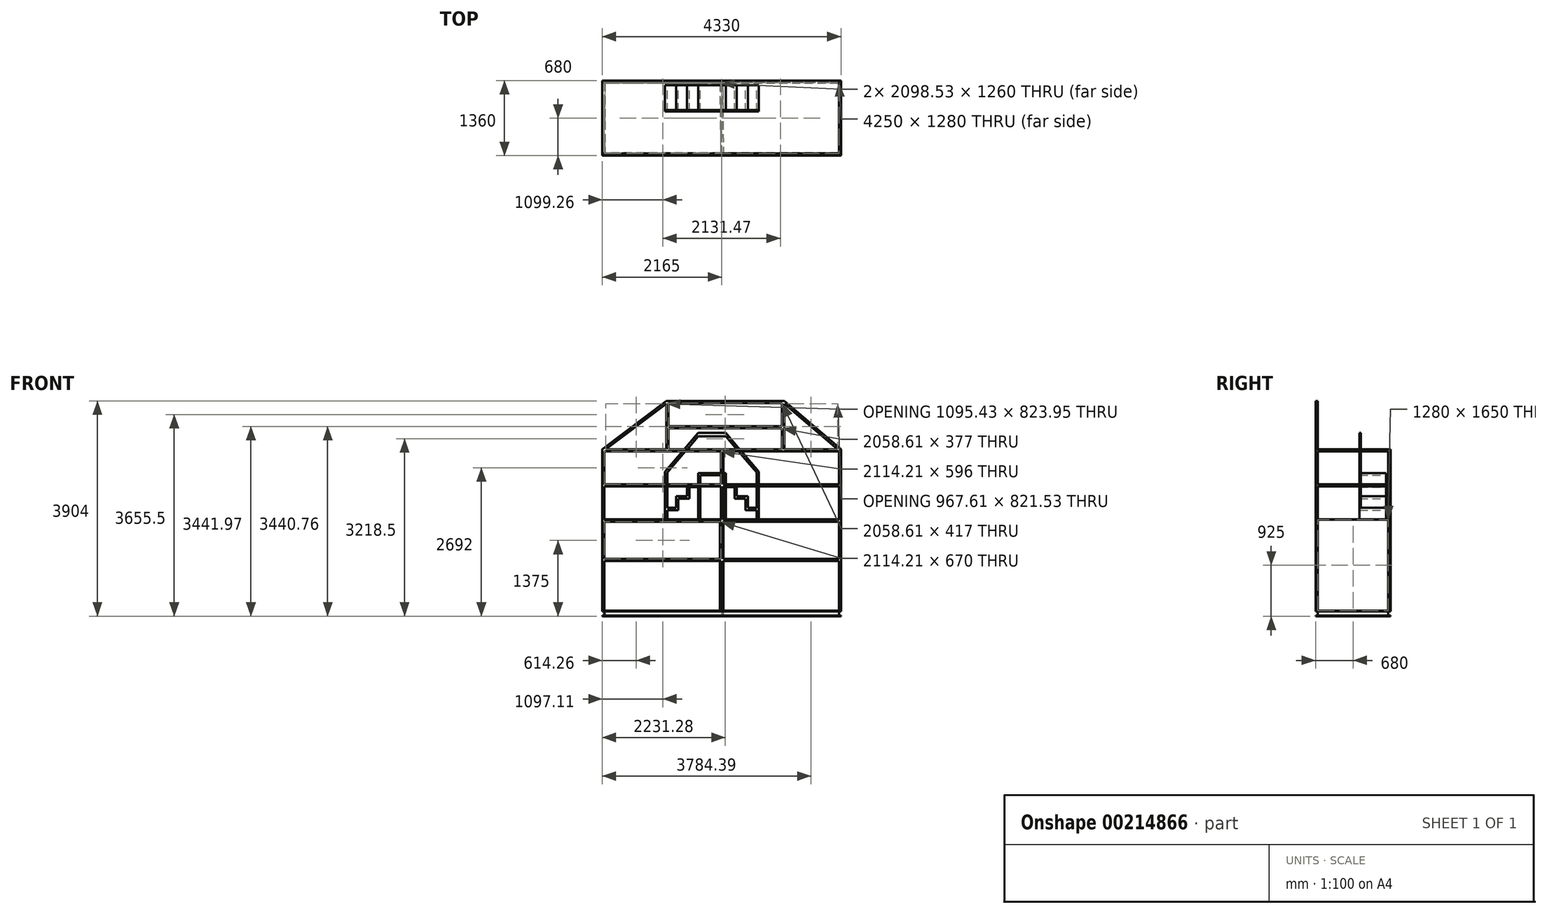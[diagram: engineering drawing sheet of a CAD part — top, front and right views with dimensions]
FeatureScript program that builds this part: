
annotation { "Feature Type Name" : "Feature", "Feature Type Description" : "" }
export const myFeature = defineFeature(function(context is Context, id is Id, definition is map)
    precondition{}
    {
        {
            var Q0;
            Q0=qCreatedBy(makeId("Top.planeOp"),FACE);
            var sketch = newSketch(context, id + "F0", { "sketchPlane" : qUnion([Q0])});
            skLineSegment(sketch, "E0.rect.bottom", {"start": v(2165, 680) * mm, "end": v(-2165, 680) * mm});
            skLineSegment(sketch, "E0.rect.top", {"start": v(2165, -680) * mm, "end": v(-2165, -680) * mm});
            skLineSegment(sketch, "E0.rect.left", {"start": v(2165, 680) * mm, "end": v(2165, -680) * mm});
            skLineSegment(sketch, "E0.rect.right", {"start": v(-2165, 680) * mm, "end": v(-2165, -680) * mm});
            skPoint(sketch, "E0.rect.middle", {"position": v(0, 0) * mm});
            skLineSegment(sketch, "E1.rect.bottom", {"start": v(2115, 630) * mm, "end": v(16.47, 630) * mm});
            skLineSegment(sketch, "E1.rect.top", {"start": v(2115, -630) * mm, "end": v(33.53, -630) * mm});
            skLineSegment(sketch, "E1.rect.left", {"start": v(2115, 630) * mm, "end": v(2115, -630) * mm});
            skLineSegment(sketch, "E1.rect.right", {"start": v(-2115, 630) * mm, "end": v(-2115, -630) * mm});
            skLineSegment(sketch, "E2.rect.left", {"start": v(16.47, 630) * mm, "end": v(33.53, -630) * mm});
            skLineSegment(sketch, "E2.rect.right", {"start": v(-33.53, 630) * mm, "end": v(-16.47, -630) * mm});
            skLineSegment(sketch, "E3.trimOffspring", {"start": v(-33.53, 630) * mm, "end": v(-2115, 630) * mm});
            skLineSegment(sketch, "E4.trimOffspring", {"start": v(-16.47, -630) * mm, "end": v(-2115, -630) * mm});
            skSolve(sketch);
        }
        {
            var Q0;
            Q0=makeQuery(id+"F0.imprint","IMPRINT",FACE,{"disambiguationData":[TD([[makeQuery(id+"F0.imprint","IMPRINT",EDGE,{"derivedFrom":sQuery(id+"F0.wireOp",EDGE,"E0.rect.bottom")}),1.0]])]});
            extrude(context, id + "F1", {"entities" : qUnion([Q0]), "depth" : 100 * mm});
        }
        {
            var Q0;
            Q0=makeQuery(id+"F1.opExtrude","SWEPT_FACE",FACE,{"disambiguationData":[OSD([sQuery(id+"F0.wireOp",EDGE,"E0.rect.right")])]});
            var sketch = newSketch(context, id + "F2", { "sketchPlane" : qUnion([Q0])});
            skLineSegment(sketch, "E5.bottom", {"start": v(-680, 90) * mm, "end": v(-640, 90) * mm});
            skLineSegment(sketch, "E5.top", {"start": v(-680, 10) * mm, "end": v(-640, 10) * mm});
            skLineSegment(sketch, "E5.left", {"start": v(-680, 90) * mm, "end": v(-680, 10) * mm});
            skLineSegment(sketch, "E5.right", {"start": v(-640, 90) * mm, "end": v(-640, 10) * mm});
            skLineSegment(sketch, "E6.bottom", {"start": v(680, 90) * mm, "end": v(640, 90) * mm});
            skLineSegment(sketch, "E6.top", {"start": v(680, 10) * mm, "end": v(640, 10) * mm});
            skLineSegment(sketch, "E6.left", {"start": v(680, 90) * mm, "end": v(680, 10) * mm});
            skLineSegment(sketch, "E6.right", {"start": v(640, 90) * mm, "end": v(640, 10) * mm});
            skSolve(sketch);
        }
        {
            var Q0;
            Q0=makeQuery(id+"F2.imprint","IMPRINT",FACE,{"disambiguationData":[TD([[makeQuery(id+"F2.imprint","IMPRINT",EDGE,{"derivedFrom":sQuery(id+"F2.wireOp",EDGE,"E5.bottom")}),-1.0]])]});
            var Q1;
            Q1=makeQuery(id+"F2.imprint","IMPRINT",FACE,{"disambiguationData":[TD([[makeQuery(id+"F2.imprint","IMPRINT",EDGE,{"derivedFrom":sQuery(id+"F2.wireOp",EDGE,"E6.bottom")}),1.0]])]});
            extrude(context, id + "F3", {"entities" : qUnion([Q0, Q1]), "operationType" : NewBodyOperationType.REMOVE, "endBound" : BoundingType.THROUGH_ALL, "oppositeDirection" : true, "depth" : 25 * mm});
        }
        {
            var Q0;
            Q0=makeQuery(id+"F3.boolean.opBoolean","COPY",FACE,{"derivedFrom":makeQuery(id+"F3.opExtrude","SWEPT_FACE",FACE,{"disambiguationData":[OSD([sQuery(id+"F2.wireOp",EDGE,"E6.right")])]})});
            var sketch = newSketch(context, id + "F4", { "sketchPlane" : qUnion([Q0])});
            skLineSegment(sketch, "E7.bottom", {"start": v(2165, 90) * mm, "end": v(2125, 90) * mm});
            skLineSegment(sketch, "E7.top", {"start": v(2165, 10) * mm, "end": v(2125, 10) * mm});
            skLineSegment(sketch, "E7.left", {"start": v(2165, 90) * mm, "end": v(2165, 10) * mm});
            skLineSegment(sketch, "E7.right", {"start": v(2125, 90) * mm, "end": v(2125, 10) * mm});
            skLineSegment(sketch, "E8.bottom", {"start": v(-2165, 90) * mm, "end": v(-2125, 90) * mm});
            skLineSegment(sketch, "E8.top", {"start": v(-2165, 10) * mm, "end": v(-2125, 10) * mm});
            skLineSegment(sketch, "E8.left", {"start": v(-2165, 90) * mm, "end": v(-2165, 10) * mm});
            skLineSegment(sketch, "E8.right", {"start": v(-2125, 90) * mm, "end": v(-2125, 10) * mm});
            skSolve(sketch);
        }
        {
            var Q0;
            Q0=makeQuery(id+"F4.imprint","IMPRINT",FACE,{"disambiguationData":[TD([[makeQuery(id+"F4.imprint","IMPRINT",EDGE,{"derivedFrom":sQuery(id+"F4.wireOp",EDGE,"E7.bottom")}),1.0]])]});
            var Q1;
            Q1=makeQuery(id+"F4.imprint","IMPRINT",FACE,{"disambiguationData":[TD([[makeQuery(id+"F4.imprint","IMPRINT",EDGE,{"derivedFrom":sQuery(id+"F4.wireOp",EDGE,"E8.bottom")}),1.0]])]});
            extrude(context, id + "F5", {"entities" : qUnion([Q0, Q1]), "operationType" : NewBodyOperationType.REMOVE, "endBound" : BoundingType.THROUGH_ALL, "oppositeDirection" : true, "depth" : 25 * mm});
        }
        {
            var Q0;
            Q0=qCreatedBy(makeId("Top.planeOp"),FACE);
            cPlane(context, id + "F6", {"entities" : qUnion([Q0]), "cplaneType" : CPlaneType.OFFSET, "offset" : 1750 * mm, "width" : 150 * mm, "height" : 150 * mm});
        }
        {
            var Q0;
            Q0=qCreatedBy(makeId("Front.planeOp"),FACE);
            var sketch = newSketch(context, id + "F7", { "sketchPlane" : qUnion([Q0])});
            skLineSegment(sketch, "E9.bottom", {"start": v(0, 10) * mm, "end": v(-90, 10) * mm});
            skLineSegment(sketch, "E9.top", {"start": v(0, 90) * mm, "end": v(-90, 90) * mm});
            skLineSegment(sketch, "E9.left", {"start": v(0, 10) * mm, "end": v(0, 90) * mm});
            skLineSegment(sketch, "E9.right", {"start": v(-90, 10) * mm, "end": v(-90, 90) * mm});
            skSolve(sketch);
        }
        {
            var Q0;
            Q0=qSketchRegion(id+"F7",true);
            var Q1;
            Q1=makeQuery(id+"F1.opExtrude","SWEPT_FACE",FACE,{"disambiguationData":[OSD([sQuery(id+"F0.wireOp",EDGE,"E3.trimOffspring")])]});
            var Q2;
            Q2=makeQuery(id+"F1.opExtrude","SWEPT_FACE",FACE,{"disambiguationData":[OSD([sQuery(id+"F0.wireOp",EDGE,"E4.trimOffspring")])]});
            extrude(context, id + "F8", {"entities" : qUnion([Q0]), "operationType" : NewBodyOperationType.REMOVE, "endBound" : BoundingType.UP_TO_SURFACE, "oppositeDirection" : true, "endBoundEntityFace" : qUnion([Q1]), "depth" : 25 * mm, "hasSecondDirection" : true, "secondDirectionBound" : SecondDirectionBoundingType.UP_TO_SURFACE, "secondDirectionOppositeDirection" : false, "secondDirectionBoundEntityFace" : qUnion([Q2]), "secondDirectionDepth" : 25 * mm});
        }
        {
            var Q0;
            Q0=makeQuery(id+"F1.opExtrude","CAP_FACE",FACE,{"disambiguationData":[OSD([sQuery(id+"F0.wireOp",EDGE,"E0.rect.bottom"),sQuery(id+"F0.wireOp",EDGE,"E0.rect.top"),sQuery(id+"F0.wireOp",EDGE,"E0.rect.left"),sQuery(id+"F0.wireOp",EDGE,"E0.rect.right"),sQuery(id+"F0.wireOp",EDGE,"E1.rect.bottom"),sQuery(id+"F0.wireOp",EDGE,"E1.rect.top"),sQuery(id+"F0.wireOp",EDGE,"E1.rect.left"),sQuery(id+"F0.wireOp",EDGE,"E1.rect.right"),sQuery(id+"F0.wireOp",EDGE,"E2.rect.left"),sQuery(id+"F0.wireOp",EDGE,"E2.rect.right"),sQuery(id+"F0.wireOp",EDGE,"E3.trimOffspring"),sQuery(id+"F0.wireOp",EDGE,"E4.trimOffspring")])],"isStart":false});
            var sketch = newSketch(context, id + "F9", { "sketchPlane" : qUnion([Q0])});
            skLineSegment(sketch, "E10.bottom", {"start": v(-2165, 680) * mm, "end": v(-2125, 680) * mm});
            skLineSegment(sketch, "E10.top", {"start": v(-2165, 640) * mm, "end": v(-2125, 640) * mm});
            skLineSegment(sketch, "E10.left", {"start": v(-2165, 680) * mm, "end": v(-2165, 640) * mm});
            skLineSegment(sketch, "E10.right", {"start": v(-2125, 680) * mm, "end": v(-2125, 640) * mm});
            skLineSegment(sketch, "E11.bottom", {"start": v(2165, 680) * mm, "end": v(2125, 680) * mm});
            skLineSegment(sketch, "E11.top", {"start": v(2165, 640) * mm, "end": v(2125, 640) * mm});
            skLineSegment(sketch, "E11.left", {"start": v(2165, 680) * mm, "end": v(2165, 640) * mm});
            skLineSegment(sketch, "E11.right", {"start": v(2125, 680) * mm, "end": v(2125, 640) * mm});
            skLineSegment(sketch, "E12.bottom", {"start": v(-29.21, 680) * mm, "end": v(10.79, 680) * mm});
            skLineSegment(sketch, "E12.top", {"start": v(-28.67, 640) * mm, "end": v(11.33, 640) * mm});
            skLineSegment(sketch, "E12.left", {"start": v(-29.21, 680) * mm, "end": v(-28.67, 640) * mm});
            skLineSegment(sketch, "E12.right", {"start": v(10.79, 680) * mm, "end": v(11.33, 640) * mm});
            skLineSegment(sketch, "E13.bottom", {"start": v(-2165, -640) * mm, "end": v(-2125, -640) * mm});
            skLineSegment(sketch, "E13.top", {"start": v(-2165, -680) * mm, "end": v(-2125, -680) * mm});
            skLineSegment(sketch, "E13.left", {"start": v(-2165, -640) * mm, "end": v(-2165, -680) * mm});
            skLineSegment(sketch, "E13.right", {"start": v(-2125, -640) * mm, "end": v(-2125, -680) * mm});
            skLineSegment(sketch, "E14.bottom", {"start": v(-10.79, -680) * mm, "end": v(29.21, -680) * mm});
            skLineSegment(sketch, "E14.top", {"start": v(-10.79, -640) * mm, "end": v(28.67, -640) * mm});
            skLineSegment(sketch, "E14.right", {"start": v(28.67, -640) * mm, "end": v(29.21, -680) * mm});
            skLineSegment(sketch, "E15.bottom", {"start": v(2165, -640) * mm, "end": v(2125, -640) * mm});
            skLineSegment(sketch, "E15.top", {"start": v(2165, -680) * mm, "end": v(2125, -680) * mm});
            skLineSegment(sketch, "E15.left", {"start": v(2165, -640) * mm, "end": v(2165, -680) * mm});
            skLineSegment(sketch, "E15.right", {"start": v(2125, -640) * mm, "end": v(2125, -680) * mm});
            skLineSegment(sketch, "E16", {"start": v(-10.79, -640) * mm, "end": v(-10.79, -680) * mm});
            skSolve(sketch);
        }
        {
            var Q0;
            Q0=makeQuery(id+"F9.imprint","IMPRINT",FACE,{"disambiguationData":[TD([[makeQuery(id+"F9.imprint","IMPRINT",EDGE,{"derivedFrom":sQuery(id+"F9.wireOp",EDGE,"E14.bottom")}),-1.0]])]});
            var Q1;
            Q1=makeQuery(id+"F9.imprint","IMPRINT",FACE,{"disambiguationData":[TD([[makeQuery(id+"F9.imprint","IMPRINT",EDGE,{"derivedFrom":sQuery(id+"F9.wireOp",EDGE,"E15.bottom")}),1.0]])]});
            var Q2;
            Q2=makeQuery(id+"F9.imprint","IMPRINT",FACE,{"disambiguationData":[TD([[makeQuery(id+"F9.imprint","IMPRINT",EDGE,{"derivedFrom":sQuery(id+"F9.wireOp",EDGE,"E13.bottom")}),-1.0]])]});
            var Q3;
            Q3=makeQuery(id+"F9.imprint","IMPRINT",FACE,{"disambiguationData":[TD([[makeQuery(id+"F9.imprint","IMPRINT",EDGE,{"derivedFrom":sQuery(id+"F9.wireOp",EDGE,"E11.bottom")}),1.0]])]});
            extrude(context, id + "F10", {"entities" : qUnion([Q0, Q1, Q2, Q3]), "operationType" : NewBodyOperationType.ADD, "depth" : 2930 * mm});
        }
        {
            var Q0;
            Q0=qCreatedBy(id+"F6.planeOp",FACE);
            var sketch = newSketch(context, id + "F11", { "sketchPlane" : qUnion([Q0])});
            skLineSegment(sketch, "E17.bottom", {"start": v(-2165, 680) * mm, "end": v(2165, 680) * mm});
            skLineSegment(sketch, "E17.top", {"start": v(-2165, -680) * mm, "end": v(2165, -680) * mm});
            skLineSegment(sketch, "E17.left", {"start": v(-2165, 680) * mm, "end": v(-2165, -680) * mm});
            skLineSegment(sketch, "E17.right", {"start": v(2165, 680) * mm, "end": v(2165, -680) * mm});
            skSolve(sketch);
        }
        {
            var Q0;
            Q0=qSketchRegion(id+"F11",true);
            extrude(context, id + "F12", {"entities" : qUnion([Q0]), "operationType" : NewBodyOperationType.ADD, "depth" : 4 * mm});
        }
        {
            var Q0;
            Q0=qSketchRegion(id+"F9",true);
            extrude(context, id + "F13", {"entities" : qUnion([Q0]), "operationType" : NewBodyOperationType.ADD, "depth" : 1650 * mm});
        }
        {
            var Q0;
            {var subQ1=sQuery(id+"F0.wireOp",EDGE,"E0.rect.right");Q0=makeQuery(id+"F12.boolean.opBoolean","MERGE",FACE,{"derivedFrom":[makeQuery(id+"F10.boolean.opBoolean","MERGE",FACE,{"derivedFrom":[makeQuery(id+"F5.boolean.opBoolean","SPLIT",FACE,{"disambiguationData":[TD([makeQuery(id+"F3.boolean.opBoolean","COPY",FACE,{"derivedFrom":makeQuery(id+"F3.opExtrude","SWEPT_FACE",FACE,{"disambiguationData":[OSD([sQuery(id+"F2.wireOp",EDGE,"E5.bottom")])]})})])],"derivedFrom":makeQuery(id+"F1.opExtrude","SWEPT_FACE",FACE,{"disambiguationData":[OSD([subQ1])]})}),makeQuery(id+"F10.opExtrude","SWEPT_FACE",FACE,{"disambiguationData":[OSD([sQuery(id+"F9.wireOp",EDGE,"E10.left")])]}),makeQuery(id+"F10.opExtrude","SWEPT_FACE",FACE,{"disambiguationData":[OSD([sQuery(id+"F9.wireOp",EDGE,"E13.left")])]})]}),makeQuery(id+"F12.opExtrude","SWEPT_FACE",FACE,{"disambiguationData":[OSD([sQuery(id+"F11.wireOp",EDGE,"E17.left")])]})]});}
            var sketch = newSketch(context, id + "F14", { "sketchPlane" : qUnion([Q0])});
            skLineSegment(sketch, "E18.bottom", {"start": v(640, 3030) * mm, "end": v(680, 3030) * mm});
            skLineSegment(sketch, "E18.top", {"start": v(640, 2990) * mm, "end": v(680, 2990) * mm});
            skLineSegment(sketch, "E18.left", {"start": v(640, 3030) * mm, "end": v(640, 2990) * mm});
            skLineSegment(sketch, "E18.right", {"start": v(680, 3030) * mm, "end": v(680, 2990) * mm});
            skLineSegment(sketch, "E19.bottom", {"start": v(-680, 1040) * mm, "end": v(640, 1040) * mm});
            skLineSegment(sketch, "E19.top", {"start": v(-680, 1000) * mm, "end": v(640, 1000) * mm});
            skLineSegment(sketch, "E19.left", {"start": v(-680, 1040) * mm, "end": v(-680, 1000) * mm});
            skLineSegment(sketch, "E19.right", {"start": v(640, 1040) * mm, "end": v(640, 1000) * mm});
            skLineSegment(sketch, "E20.bottom", {"start": v(640, 1040) * mm, "end": v(680, 1040) * mm});
            skLineSegment(sketch, "E20.top", {"start": v(640, 1000) * mm, "end": v(680, 1000) * mm});
            skLineSegment(sketch, "E20.right", {"start": v(680, 1040) * mm, "end": v(680, 1000) * mm});
            skLineSegment(sketch, "E21.bottom", {"start": v(640, 2394) * mm, "end": v(680, 2394) * mm});
            skLineSegment(sketch, "E21.top", {"start": v(640, 2354) * mm, "end": v(680, 2354) * mm});
            skLineSegment(sketch, "E21.left", {"start": v(640, 2394) * mm, "end": v(640, 2354) * mm});
            skLineSegment(sketch, "E21.right", {"start": v(680, 2394) * mm, "end": v(680, 2354) * mm});
            skLineSegment(sketch, "E22.bottom", {"start": v(640, 1750) * mm, "end": v(680, 1750) * mm});
            skLineSegment(sketch, "E22.top", {"start": v(640, 1710) * mm, "end": v(680, 1710) * mm});
            skLineSegment(sketch, "E22.left", {"start": v(640, 1750) * mm, "end": v(640, 1710) * mm});
            skLineSegment(sketch, "E22.right", {"start": v(680, 1750) * mm, "end": v(680, 1710) * mm});
            skLineSegment(sketch, "E23.bottom", {"start": v(-640, 1750) * mm, "end": v(-680, 1750) * mm});
            skLineSegment(sketch, "E23.top", {"start": v(-640, 1710) * mm, "end": v(-680, 1710) * mm});
            skLineSegment(sketch, "E23.left", {"start": v(-640, 1750) * mm, "end": v(-640, 1710) * mm});
            skLineSegment(sketch, "E23.right", {"start": v(-680, 1750) * mm, "end": v(-680, 1710) * mm});
            skSolve(sketch);
        }
        {
            var Q0;
            Q0=makeQuery(id+"F14.imprint","IMPRINT",FACE,{"disambiguationData":[TD([[makeQuery(id+"F14.imprint","IMPRINT",EDGE,{"derivedFrom":sQuery(id+"F14.wireOp",EDGE,"E18.bottom")}),-1.0]])]});
            var Q1;
            Q1=makeQuery(id+"F14.imprint","IMPRINT",FACE,{"disambiguationData":[TD([[makeQuery(id+"F14.imprint","IMPRINT",EDGE,{"derivedFrom":sQuery(id+"F14.wireOp",EDGE,"E21.bottom")}),-1.0]])]});
            var Q2;
            Q2=makeQuery(id+"F14.imprint","IMPRINT",FACE,{"disambiguationData":[TD([[makeQuery(id+"F14.imprint","IMPRINT",EDGE,{"derivedFrom":sQuery(id+"F14.wireOp",EDGE,"E20.bottom")}),-1.0]])]});
            var Q3;
            {var subQ0=sQuery(id+"F14.wireOp",EDGE,"E19.left");Q3=makeQuery(id+"F14.imprint","IMPRINT",FACE,{"disambiguationData":[TD([[makeQuery(id+"F14.imprint","IMPRINT",EDGE,{"derivedFrom":subQ0}),1.0]])]});}
            var Q4;
            Q4=makeQuery(id+"F14.imprint","IMPRINT",FACE,{"disambiguationData":[TD([[makeQuery(id+"F14.imprint","IMPRINT",EDGE,{"derivedFrom":sQuery(id+"F14.wireOp",EDGE,"E22.bottom")}),-1.0]])]});
            var Q5;
            Q5=makeQuery(id+"F14.imprint","IMPRINT",FACE,{"disambiguationData":[TD([[makeQuery(id+"F14.imprint","IMPRINT",EDGE,{"derivedFrom":sQuery(id+"F14.wireOp",EDGE,"E23.bottom")}),1.0]])]});
            extrude(context, id + "F15", {"entities" : qUnion([Q0, Q1, Q2, Q3, Q4, Q5]), "operationType" : NewBodyOperationType.ADD, "oppositeDirection" : true, "depth" : 4300 * mm});
        }
        {
            var Q0;
            Q0=makeQuery(id+"F15.boolean.opBoolean","MERGE",FACE,{"derivedFrom":[makeQuery(id+"F12.boolean.opBoolean","MERGE",FACE,{"derivedFrom":[makeQuery(id+"F10.opExtrude","SWEPT_FACE",FACE,{"disambiguationData":[OSD([sQuery(id+"F9.wireOp",EDGE,"E13.top")])]}),makeQuery(id+"F10.opExtrude","SWEPT_FACE",FACE,{"disambiguationData":[OSD([sQuery(id+"F9.wireOp",EDGE,"E14.top")])]}),makeQuery(id+"F10.opExtrude","SWEPT_FACE",FACE,{"disambiguationData":[OSD([sQuery(id+"F9.wireOp",EDGE,"E15.top")])]}),makeQuery(id+"F12.opExtrude","SWEPT_FACE",FACE,{"disambiguationData":[OSD([sQuery(id+"F11.wireOp",EDGE,"E17.top")])]})]}),makeQuery(id+"F15.opExtrude","SWEPT_FACE",FACE,{"disambiguationData":[OSD([sQuery(id+"F14.wireOp",EDGE,"E18.right")])]}),makeQuery(id+"F15.opExtrude","SWEPT_FACE",FACE,{"disambiguationData":[OSD([sQuery(id+"F14.wireOp",EDGE,"E20.right")])]}),makeQuery(id+"F15.opExtrude","SWEPT_FACE",FACE,{"disambiguationData":[OSD([sQuery(id+"F14.wireOp",EDGE,"E21.right")])]})]});
            var sketch = newSketch(context, id + "F16", { "sketchPlane" : qUnion([Q0])});
            skLineSegment(sketch, "E24.bottom", {"start": v(-2165, 3030) * mm, "end": v(-2125, 3030) * mm});
            skLineSegment(sketch, "E24.top", {"start": v(-2165, 2990) * mm, "end": v(-2125, 2990) * mm});
            skLineSegment(sketch, "E24.left", {"start": v(-2165, 3030) * mm, "end": v(-2165, 2990) * mm});
            skLineSegment(sketch, "E24.right", {"start": v(-2125, 3030) * mm, "end": v(-2125, 2990) * mm});
            skLineSegment(sketch, "E25.bottom", {"start": v(-2125, 2394) * mm, "end": v(-2165, 2394) * mm});
            skLineSegment(sketch, "E25.top", {"start": v(-2125, 2354) * mm, "end": v(-2165, 2354) * mm});
            skLineSegment(sketch, "E25.left", {"start": v(-2125, 2394) * mm, "end": v(-2125, 2354) * mm});
            skLineSegment(sketch, "E25.right", {"start": v(-2165, 2394) * mm, "end": v(-2165, 2354) * mm});
            skLineSegment(sketch, "E26.bottom", {"start": v(2125, 2394) * mm, "end": v(2165, 2394) * mm});
            skLineSegment(sketch, "E26.top", {"start": v(2125, 2354) * mm, "end": v(2165, 2354) * mm});
            skLineSegment(sketch, "E26.left", {"start": v(2125, 2394) * mm, "end": v(2125, 2354) * mm});
            skLineSegment(sketch, "E26.right", {"start": v(2165, 2394) * mm, "end": v(2165, 2354) * mm});
            skLineSegment(sketch, "E27.bottom", {"start": v(2125, 2990) * mm, "end": v(2165, 2990) * mm});
            skLineSegment(sketch, "E27.top", {"start": v(2125, 3030) * mm, "end": v(2165, 3030) * mm});
            skLineSegment(sketch, "E27.left", {"start": v(2125, 2990) * mm, "end": v(2125, 3030) * mm});
            skLineSegment(sketch, "E27.right", {"start": v(2165, 2990) * mm, "end": v(2165, 3030) * mm});
            skSolve(sketch);
        }
        {
            var Q0;
            Q0=makeQuery(id+"F16.imprint","IMPRINT",FACE,{"disambiguationData":[TD([[makeQuery(id+"F16.imprint","IMPRINT",EDGE,{"derivedFrom":sQuery(id+"F16.wireOp",EDGE,"E26.bottom")}),-1.0]])]});
            var Q1;
            Q1=makeQuery(id+"F16.imprint","IMPRINT",FACE,{"disambiguationData":[TD([[makeQuery(id+"F16.imprint","IMPRINT",EDGE,{"derivedFrom":sQuery(id+"F16.wireOp",EDGE,"E27.bottom")}),1.0]])]});
            var Q2;
            {var subQ0=sQuery(id+"F9.wireOp",EDGE,"E11.right");var subQ1=sQuery(id+"F9.wireOp",EDGE,"E11.left");var subQ2=sQuery(id+"F9.wireOp",EDGE,"E11.top");Q2=makeQuery(id+"F12.boolean.opBoolean","SPLIT",FACE,{"disambiguationData":[TD([makeQuery(id+"F10.opExtrude","CAP_FACE",FACE,{"disambiguationData":[OSD([sQuery(id+"F9.wireOp",EDGE,"E11.bottom"),subQ2,subQ1,subQ0])],"isStart":false})])],"derivedFrom":makeQuery(id+"F10.opExtrude","SWEPT_FACE",FACE,{"disambiguationData":[OSD([subQ2])]})});}
            extrude(context, id + "F17", {"entities" : qUnion([Q0, Q1]), "operationType" : NewBodyOperationType.ADD, "endBound" : BoundingType.UP_TO_SURFACE, "oppositeDirection" : true, "endBoundEntityFace" : qUnion([Q2]), "depth" : 920 * mm});
        }
        {
            var Q0;
            Q0=qCreatedBy(makeId("Front.planeOp"),FACE);
            cPlane(context, id + "F18", {"entities" : qUnion([Q0]), "cplaneType" : CPlaneType.OFFSET, "offset" : 600 * mm, "oppositeDirection" : true, "width" : 150 * mm, "height" : 150 * mm});
        }
        {
            var Q0;
            Q0=qCreatedBy(id+"F18.planeOp",FACE);
            var sketch = newSketch(context, id + "F19", { "sketchPlane" : qUnion([Q0])});
            skLineSegment(sketch, "E28", {"start": v(73.97, 1754) * mm, "end": v(73.97, 2594) * mm});
            skLineSegment(sketch, "E29", {"start": v(73.97, 2594) * mm, "end": v(-426.03, 2594) * mm});
            skLineSegment(sketch, "E30", {"start": v(-426.03, 2594) * mm, "end": v(-426.03, 1754) * mm});
            skLineSegment(sketch, "E31", {"start": v(-426.03, 1754) * mm, "end": v(-386.03, 1754) * mm});
            skLineSegment(sketch, "E32", {"start": v(-386.03, 1754) * mm, "end": v(-386.03, 2554) * mm});
            skLineSegment(sketch, "E33", {"start": v(-386.03, 2554) * mm, "end": v(33.97, 2554) * mm});
            skLineSegment(sketch, "E34", {"start": v(33.97, 2554) * mm, "end": v(33.97, 1754) * mm});
            skLineSegment(sketch, "E35", {"start": v(33.97, 1754) * mm, "end": v(73.97, 1754) * mm});
            skLineSegment(sketch, "E36", {"start": v(73.97, 2384) * mm, "end": v(273.97, 2384) * mm});
            skLineSegment(sketch, "E37", {"start": v(273.97, 2384) * mm, "end": v(273.97, 2174) * mm});
            skLineSegment(sketch, "E38", {"start": v(273.97, 2174) * mm, "end": v(473.97, 2174) * mm});
            skLineSegment(sketch, "E39", {"start": v(473.97, 2174) * mm, "end": v(473.97, 1964) * mm});
            skLineSegment(sketch, "E40", {"start": v(473.97, 1964) * mm, "end": v(433.97, 1964) * mm});
            skLineSegment(sketch, "E41", {"start": v(433.97, 1964) * mm, "end": v(433.97, 2134) * mm});
            skLineSegment(sketch, "E42", {"start": v(433.97, 2134) * mm, "end": v(233.97, 2134) * mm});
            skLineSegment(sketch, "E43", {"start": v(233.97, 2134) * mm, "end": v(233.97, 2344) * mm});
            skLineSegment(sketch, "E44", {"start": v(233.97, 2344) * mm, "end": v(73.97, 2344) * mm});
            skLineSegment(sketch, "E45", {"start": v(-176.03, 2594) * mm, "end": v(-176.03, 2051.5) * mm, "construction": true});
            skLineSegment(sketch, "E46.MirrorCS", {"start": v(-586.03, 2344) * mm, "end": v(-426.03, 2344) * mm});
            skLineSegment(sketch, "E47.MirrorCS", {"start": v(-426.03, 2384) * mm, "end": v(-626.03, 2384) * mm});
            skLineSegment(sketch, "E48.MirrorCS", {"start": v(-626.03, 2384) * mm, "end": v(-626.03, 2174) * mm});
            skLineSegment(sketch, "E49.MirrorCS", {"start": v(-786.03, 2134) * mm, "end": v(-586.03, 2134) * mm});
            skLineSegment(sketch, "E50.MirrorCS", {"start": v(-626.03, 2174) * mm, "end": v(-826.03, 2174) * mm});
            skLineSegment(sketch, "E51.MirrorCS", {"start": v(-826.03, 2174) * mm, "end": v(-826.03, 1964) * mm});
            skLineSegment(sketch, "E52.MirrorCS", {"start": v(-786.03, 1964) * mm, "end": v(-786.03, 2134) * mm});
            skLineSegment(sketch, "E53.MirrorCS", {"start": v(-586.03, 2134) * mm, "end": v(-586.03, 2344) * mm});
            skLineSegment(sketch, "E54.MirrorCS", {"start": v(-826.03, 1964) * mm, "end": v(-786.03, 1964) * mm});
            skLineSegment(sketch, "E55", {"start": v(473.97, 1964) * mm, "end": v(673.97, 1964) * mm});
            skLineSegment(sketch, "E56", {"start": v(673.97, 1964) * mm, "end": v(673.97, 1754) * mm});
            skLineSegment(sketch, "E57", {"start": v(673.97, 1754) * mm, "end": v(633.97, 1754) * mm});
            skLineSegment(sketch, "E58", {"start": v(633.97, 1754) * mm, "end": v(633.97, 1924) * mm});
            skLineSegment(sketch, "E59", {"start": v(633.97, 1924) * mm, "end": v(433.97, 1924) * mm});
            skLineSegment(sketch, "E60", {"start": v(433.97, 1924) * mm, "end": v(433.97, 1964) * mm});
            skLineSegment(sketch, "E61.MirrorCS", {"start": v(-986.03, 1924) * mm, "end": v(-786.03, 1924) * mm});
            skLineSegment(sketch, "E62.MirrorCS", {"start": v(-826.03, 1964) * mm, "end": v(-1026.03, 1964) * mm});
            skLineSegment(sketch, "E63.MirrorCS", {"start": v(-1026.03, 1964) * mm, "end": v(-1026.03, 1754) * mm});
            skLineSegment(sketch, "E64.MirrorCS", {"start": v(-986.03, 1754) * mm, "end": v(-986.03, 1924) * mm});
            skLineSegment(sketch, "E65.MirrorCS", {"start": v(-786.03, 1924) * mm, "end": v(-786.03, 1964) * mm});
            skLineSegment(sketch, "E66.MirrorCS", {"start": v(-1026.03, 1754) * mm, "end": v(-986.03, 1754) * mm});
            skSolve(sketch);
        }
        {
            var Q0;
            {var subQ1=sQuery(id+"F19.wireOp",EDGE,"QDDcSzbj-dvXj-XOp7-vtiu-wOcYaTmfimKI");Q0=makeQuery(id+"F19.imprint","IMPRINT",FACE,{"disambiguationData":[TD([[makeQuery(id+"F19.imprint","IMPRINT",EDGE,{"derivedFrom":subQ1}),-1.0]])]});}
            var Q1;
            {var subQ0=sQuery(id+"F19.wireOp",EDGE,"E29");Q1=makeQuery(id+"F19.imprint","IMPRINT",FACE,{"disambiguationData":[TD([[makeQuery(id+"F19.imprint","IMPRINT",EDGE,{"derivedFrom":subQ0}),1.0]])]});}
            var Q2;
            {var subQ1=sQuery(id+"F19.wireOp",EDGE,"Bypho93v-gEm8-qDYy-SaEK-ACIk8DJtcY5p");Q2=makeQuery(id+"F19.imprint","IMPRINT",FACE,{"disambiguationData":[TD([[makeQuery(id+"F19.imprint","IMPRINT",EDGE,{"derivedFrom":subQ1}),1.0]])]});}
            var Q3;
            {var subQ0=sQuery(id+"F19.wireOp",EDGE,"E36");Q3=makeQuery(id+"F19.imprint","IMPRINT",FACE,{"disambiguationData":[TD([[makeQuery(id+"F19.imprint","IMPRINT",EDGE,{"derivedFrom":subQ0}),-1.0]])]});}
            var Q4;
            {var subQ1=sQuery(id+"F19.wireOp",EDGE,"E46.MirrorCS");Q4=makeQuery(id+"F19.imprint","IMPRINT",FACE,{"disambiguationData":[TD([[makeQuery(id+"F19.imprint","IMPRINT",EDGE,{"derivedFrom":subQ1}),1.0]])]});}
            var Q5;
            Q5=makeQuery(id+"F19.imprint","IMPRINT",FACE,{"disambiguationData":[TD([[makeQuery(id+"F19.imprint","IMPRINT",EDGE,{"derivedFrom":sQuery(id+"F19.wireOp",EDGE,"E40")}),1.0]])]});
            var Q6;
            Q6=makeQuery(id+"F19.imprint","IMPRINT",FACE,{"disambiguationData":[TD([[makeQuery(id+"F19.imprint","IMPRINT",EDGE,{"derivedFrom":sQuery(id+"F19.wireOp",EDGE,"E54.MirrorCS")}),-1.0]])]});
            extrude(context, id + "F20", {"entities" : qUnion([Q0, Q1, Q2, Q3, Q4, Q5, Q6]), "operationType" : NewBodyOperationType.ADD, "depth" : 480 * mm});
        }
        {
            var Q0;
            Q0=makeQuery(id+"F15.boolean.opBoolean","MERGE",FACE,{"derivedFrom":[makeQuery(id+"F12.boolean.opBoolean","MERGE",FACE,{"derivedFrom":[makeQuery(id+"F10.opExtrude","SWEPT_FACE",FACE,{"disambiguationData":[OSD([sQuery(id+"F9.wireOp",EDGE,"E13.top")])]}),makeQuery(id+"F10.opExtrude","SWEPT_FACE",FACE,{"disambiguationData":[OSD([sQuery(id+"F9.wireOp",EDGE,"E14.top")])]}),makeQuery(id+"F10.opExtrude","SWEPT_FACE",FACE,{"disambiguationData":[OSD([sQuery(id+"F9.wireOp",EDGE,"E15.top")])]}),makeQuery(id+"F12.opExtrude","SWEPT_FACE",FACE,{"disambiguationData":[OSD([sQuery(id+"F11.wireOp",EDGE,"E17.top")])]})]}),makeQuery(id+"F15.opExtrude","SWEPT_FACE",FACE,{"disambiguationData":[OSD([sQuery(id+"F14.wireOp",EDGE,"E18.right")])]}),makeQuery(id+"F15.opExtrude","SWEPT_FACE",FACE,{"disambiguationData":[OSD([sQuery(id+"F14.wireOp",EDGE,"E20.right")])]}),makeQuery(id+"F15.opExtrude","SWEPT_FACE",FACE,{"disambiguationData":[OSD([sQuery(id+"F14.wireOp",EDGE,"E21.right")])]})]});
            var sketch = newSketch(context, id + "F21", { "sketchPlane" : qUnion([Q0])});
            skLineSegment(sketch, "E67", {"start": v(-1003.02, 3030) * mm, "end": v(-1003.02, 3904) * mm});
            skLineSegment(sketch, "E68", {"start": v(-1003.02, 3904) * mm, "end": v(1135.58, 3904) * mm});
            skLineSegment(sketch, "E69", {"start": v(1135.58, 3904) * mm, "end": v(1135.58, 3030) * mm});
            skLineSegment(sketch, "E70", {"start": v(-1003.02, 3904) * mm, "end": v(-2165, 3030) * mm});
            skLineSegment(sketch, "E71", {"start": v(1135.58, 3904) * mm, "end": v(2165, 3030) * mm});
            skLineSegment(sketch, "E72", {"start": v(-963.02, 3030) * mm, "end": v(-963.02, 3864) * mm});
            skLineSegment(sketch, "E73", {"start": v(-963.02, 3864) * mm, "end": v(1095.58, 3864) * mm});
            skLineSegment(sketch, "E74", {"start": v(1095.58, 3864) * mm, "end": v(1095.58, 3030) * mm});
            skLineSegment(sketch, "E75", {"start": v(-1003.02, 3853.95) * mm, "end": v(-2098.46, 3030) * mm});
            skLineSegment(sketch, "E76", {"start": v(1135.58, 3851.53) * mm, "end": v(2103.2, 3030) * mm});
            skLineSegment(sketch, "E77", {"start": v(-963.02, 3447) * mm, "end": v(1095.58, 3447) * mm});
            skLineSegment(sketch, "E78", {"start": v(-963.02, 3407) * mm, "end": v(1095.58, 3407) * mm});
            skSolve(sketch);
        }
        {
            var Q0;
            {var subQ0=sQuery(id+"F21.wireOp",EDGE,"E70");Q0=makeQuery(id+"F21.imprint","IMPRINT",FACE,{"disambiguationData":[TD([[makeQuery(id+"F21.imprint","IMPRINT",EDGE,{"derivedFrom":subQ0}),1.0]])]});}
            var Q1;
            {var subQ16=sQuery(id+"F21.wireOp",EDGE,"E68");Q1=makeQuery(id+"F21.imprint","IMPRINT",FACE,{"disambiguationData":[TD([[makeQuery(id+"F21.imprint","IMPRINT",EDGE,{"derivedFrom":subQ16}),-1.0]])]});}
            var Q2;
            {var subQ0=sQuery(id+"F21.wireOp",EDGE,"E77");Q2=makeQuery(id+"F21.imprint","IMPRINT",FACE,{"disambiguationData":[TD([[makeQuery(id+"F21.imprint","IMPRINT",EDGE,{"derivedFrom":subQ0}),-1.0]])]});}
            var Q3;
            {var subQ0=sQuery(id+"F21.wireOp",EDGE,"E71");Q3=makeQuery(id+"F21.imprint","IMPRINT",FACE,{"disambiguationData":[TD([[makeQuery(id+"F21.imprint","IMPRINT",EDGE,{"derivedFrom":subQ0}),-1.0]])]});}
            extrude(context, id + "F22", {"entities" : qUnion([Q0, Q1, Q2, Q3]), "operationType" : NewBodyOperationType.ADD, "oppositeDirection" : true, "depth" : 40 * mm});
        }
        {
            var Q0;
            {var subQ0=sQuery(id+"F14.wireOp",EDGE,"E18.right");var subQ1=sQuery(id+"F9.wireOp",EDGE,"E15.top");var subQ2=sQuery(id+"F9.wireOp",EDGE,"E14.top");var subQ3=sQuery(id+"F9.wireOp",EDGE,"E13.top");Q0=makeQuery(id+"F22.boolean.opBoolean","MERGE",FACE,{"derivedFrom":[makeQuery(id+"F15.boolean.opBoolean","MERGE",FACE,{"derivedFrom":[makeQuery(id+"F12.boolean.opBoolean","MERGE",FACE,{"derivedFrom":[makeQuery(id+"F10.opExtrude","SWEPT_FACE",FACE,{"disambiguationData":[OSD([subQ3])]}),makeQuery(id+"F10.opExtrude","SWEPT_FACE",FACE,{"disambiguationData":[OSD([subQ2])]}),makeQuery(id+"F10.opExtrude","SWEPT_FACE",FACE,{"disambiguationData":[OSD([subQ1])]}),makeQuery(id+"F12.opExtrude","SWEPT_FACE",FACE,{"disambiguationData":[OSD([sQuery(id+"F11.wireOp",EDGE,"E17.top")])]})]}),makeQuery(id+"F15.opExtrude","SWEPT_FACE",FACE,{"disambiguationData":[OSD([subQ0])]}),makeQuery(id+"F15.opExtrude","SWEPT_FACE",FACE,{"disambiguationData":[OSD([sQuery(id+"F14.wireOp",EDGE,"E20.right")])]}),makeQuery(id+"F15.opExtrude","SWEPT_FACE",FACE,{"disambiguationData":[OSD([sQuery(id+"F14.wireOp",EDGE,"E21.right")])]})]}),makeQuery(id+"F22.opExtrude","CAP_FACE",FACE,{"disambiguationData":[OSD([subQ3,subQ2,subQ1,sQuery(id+"F14.wireOp",EDGE,"E18.bottom"),subQ0,sQuery(id+"F21.wireOp",EDGE,"E67"),sQuery(id+"F21.wireOp",EDGE,"E68"),sQuery(id+"F21.wireOp",EDGE,"E69"),sQuery(id+"F21.wireOp",EDGE,"E70"),sQuery(id+"F21.wireOp",EDGE,"E71"),sQuery(id+"F21.wireOp",EDGE,"E72"),sQuery(id+"F21.wireOp",EDGE,"E73"),sQuery(id+"F21.wireOp",EDGE,"E74"),sQuery(id+"F21.wireOp",EDGE,"E75"),sQuery(id+"F21.wireOp",EDGE,"E76"),sQuery(id+"F21.wireOp",EDGE,"E77"),sQuery(id+"F21.wireOp",EDGE,"E78")])],"isStart":true})]});}
            var sketch = newSketch(context, id + "F23", { "sketchPlane" : qUnion([Q0])});
            skLineSegment(sketch, "E79.bottom", {"start": v(2125, 2990) * mm, "end": v(2165, 2990) * mm});
            skLineSegment(sketch, "E79.top", {"start": v(2125, 3030) * mm, "end": v(2165, 3030) * mm});
            skLineSegment(sketch, "E79.left", {"start": v(2125, 2990) * mm, "end": v(2125, 3030) * mm});
            skLineSegment(sketch, "E79.right", {"start": v(2165, 2990) * mm, "end": v(2165, 3030) * mm});
            skSolve(sketch);
        }
        {
            var Q0;
            Q0=makeQuery(id+"F23.imprint","IMPRINT",FACE,{"disambiguationData":[TD([[makeQuery(id+"F23.imprint","IMPRINT",EDGE,{"derivedFrom":sQuery(id+"F23.wireOp",EDGE,"E79.bottom")}),1.0]])]});
            extrude(context, id + "F24", {"entities" : qUnion([Q0]), "operationType" : NewBodyOperationType.ADD, "oppositeDirection" : true, "depth" : 240 * mm});
        }
        {
            var Q0;
            Q0=makeQuery(id+"F20.opExtrude","CAP_FACE",FACE,{"disambiguationData":[OSD([sQuery(id+"F19.wireOp",EDGE,"E28"),sQuery(id+"F19.wireOp",EDGE,"E29"),sQuery(id+"F19.wireOp",EDGE,"E30"),sQuery(id+"F19.wireOp",EDGE,"E31"),sQuery(id+"F19.wireOp",EDGE,"E32"),sQuery(id+"F19.wireOp",EDGE,"E33"),sQuery(id+"F19.wireOp",EDGE,"E34"),sQuery(id+"F19.wireOp",EDGE,"E35"),sQuery(id+"F19.wireOp",EDGE,"E36"),sQuery(id+"F19.wireOp",EDGE,"E37"),sQuery(id+"F19.wireOp",EDGE,"E38"),sQuery(id+"F19.wireOp",EDGE,"E39"),sQuery(id+"F19.wireOp",EDGE,"E41"),sQuery(id+"F19.wireOp",EDGE,"E42"),sQuery(id+"F19.wireOp",EDGE,"E43"),sQuery(id+"F19.wireOp",EDGE,"E44"),sQuery(id+"F19.wireOp",EDGE,"E46.MirrorCS"),sQuery(id+"F19.wireOp",EDGE,"E47.MirrorCS"),sQuery(id+"F19.wireOp",EDGE,"E48.MirrorCS"),sQuery(id+"F19.wireOp",EDGE,"E49.MirrorCS"),sQuery(id+"F19.wireOp",EDGE,"E50.MirrorCS"),sQuery(id+"F19.wireOp",EDGE,"E51.MirrorCS"),sQuery(id+"F19.wireOp",EDGE,"E52.MirrorCS"),sQuery(id+"F19.wireOp",EDGE,"E53.MirrorCS"),sQuery(id+"F19.wireOp",EDGE,"E55"),sQuery(id+"F19.wireOp",EDGE,"E56"),sQuery(id+"F19.wireOp",EDGE,"E57"),sQuery(id+"F19.wireOp",EDGE,"E58"),sQuery(id+"F19.wireOp",EDGE,"E59"),sQuery(id+"F19.wireOp",EDGE,"E60"),sQuery(id+"F19.wireOp",EDGE,"E61.MirrorCS"),sQuery(id+"F19.wireOp",EDGE,"E62.MirrorCS"),sQuery(id+"F19.wireOp",EDGE,"E63.MirrorCS"),sQuery(id+"F19.wireOp",EDGE,"E64.MirrorCS"),sQuery(id+"F19.wireOp",EDGE,"E65.MirrorCS"),sQuery(id+"F19.wireOp",EDGE,"E66.MirrorCS")])],"isStart":false});
            var sketch = newSketch(context, id + "F25", { "sketchPlane" : qUnion([Q0])});
            skPoint(sketch, "E80.endSnap0", {"position": v(73.97, 2489) * mm});
            skLineSegment(sketch, "E81", {"start": v(-1026.03, 1964) * mm, "end": v(-986.03, 1964) * mm});
            skLineSegment(sketch, "E82", {"start": v(633.97, 1964) * mm, "end": v(673.97, 1964) * mm});
            skLineSegment(sketch, "E83", {"start": v(-176.03, 2594) * mm, "end": v(-176.03, 3602.47) * mm, "construction": true});
            skLineSegment(sketch, "E84", {"start": v(73.97, 2594) * mm, "end": v(73.97, 3668.56) * mm, "construction": true});
            skLineSegment(sketch, "E85", {"start": v(-426.03, 2594) * mm, "end": v(-426.03, 3603.3) * mm, "construction": true});
            skLineSegment(sketch, "E86", {"start": v(-1026.03, 1964) * mm, "end": v(-1026.03, 2623.44) * mm});
            skLineSegment(sketch, "E87", {"start": v(-1026.03, 2623.44) * mm, "end": v(-426.03, 3323.56) * mm});
            skLineSegment(sketch, "E88", {"start": v(-426.03, 3323.56) * mm, "end": v(-176.03, 3323.56) * mm});
            skLineSegment(sketch, "E89", {"start": v(-176.03, 3323.56) * mm, "end": v(-176.03, 3262.1) * mm});
            skLineSegment(sketch, "E90", {"start": v(-176.03, 3262.1) * mm, "end": v(-426.03, 3262.1) * mm});
            skLineSegment(sketch, "E91", {"start": v(-426.03, 3262.1) * mm, "end": v(-986.03, 2608.64) * mm});
            skLineSegment(sketch, "E92", {"start": v(-986.03, 2608.64) * mm, "end": v(-986.03, 1964) * mm});
            skLineSegment(sketch, "E93.MirrorCS", {"start": v(-176.03, 3262.1) * mm, "end": v(73.97, 3262.1) * mm});
            skLineSegment(sketch, "E94.MirrorCS", {"start": v(73.97, 3323.56) * mm, "end": v(-176.03, 3323.56) * mm});
            skLineSegment(sketch, "E95.MirrorCS", {"start": v(673.97, 2623.44) * mm, "end": v(73.97, 3323.56) * mm});
            skLineSegment(sketch, "E96.MirrorCS", {"start": v(73.97, 3262.1) * mm, "end": v(633.97, 2608.64) * mm});
            skLineSegment(sketch, "E97.MirrorCS", {"start": v(673.97, 1964) * mm, "end": v(673.97, 2623.44) * mm});
            skLineSegment(sketch, "E98.MirrorCS", {"start": v(633.97, 2608.64) * mm, "end": v(633.97, 1964) * mm});
            skSolve(sketch);
        }
        {
            var Q0;
            Q0=makeQuery(id+"F25.imprint","IMPRINT",FACE,{"disambiguationData":[TD([[makeQuery(id+"F25.imprint","IMPRINT",EDGE,{"derivedFrom":sQuery(id+"F25.wireOp",EDGE,"kj9H4cpo-WZYA-L58w-gy0i-ARGhy10xVLZ4")}),-1.0]])]});
            var Q1;
            Q1=makeQuery(id+"F25.imprint","IMPRINT",FACE,{"disambiguationData":[TD([[makeQuery(id+"F25.imprint","IMPRINT",EDGE,{"derivedFrom":sQuery(id+"F25.wireOp",EDGE,"E81")}),-1.0]])]});
            var Q2;
            Q2=makeQuery(id+"F25.imprint","IMPRINT",FACE,{"disambiguationData":[TD([[makeQuery(id+"F25.imprint","IMPRINT",EDGE,{"derivedFrom":sQuery(id+"F25.wireOp",EDGE,"E82")}),1.0]])]});
            extrude(context, id + "F26", {"entities" : qUnion([Q0, Q1, Q2]), "operationType" : NewBodyOperationType.ADD, "oppositeDirection" : true, "depth" : 25 * mm});
        }
    });
